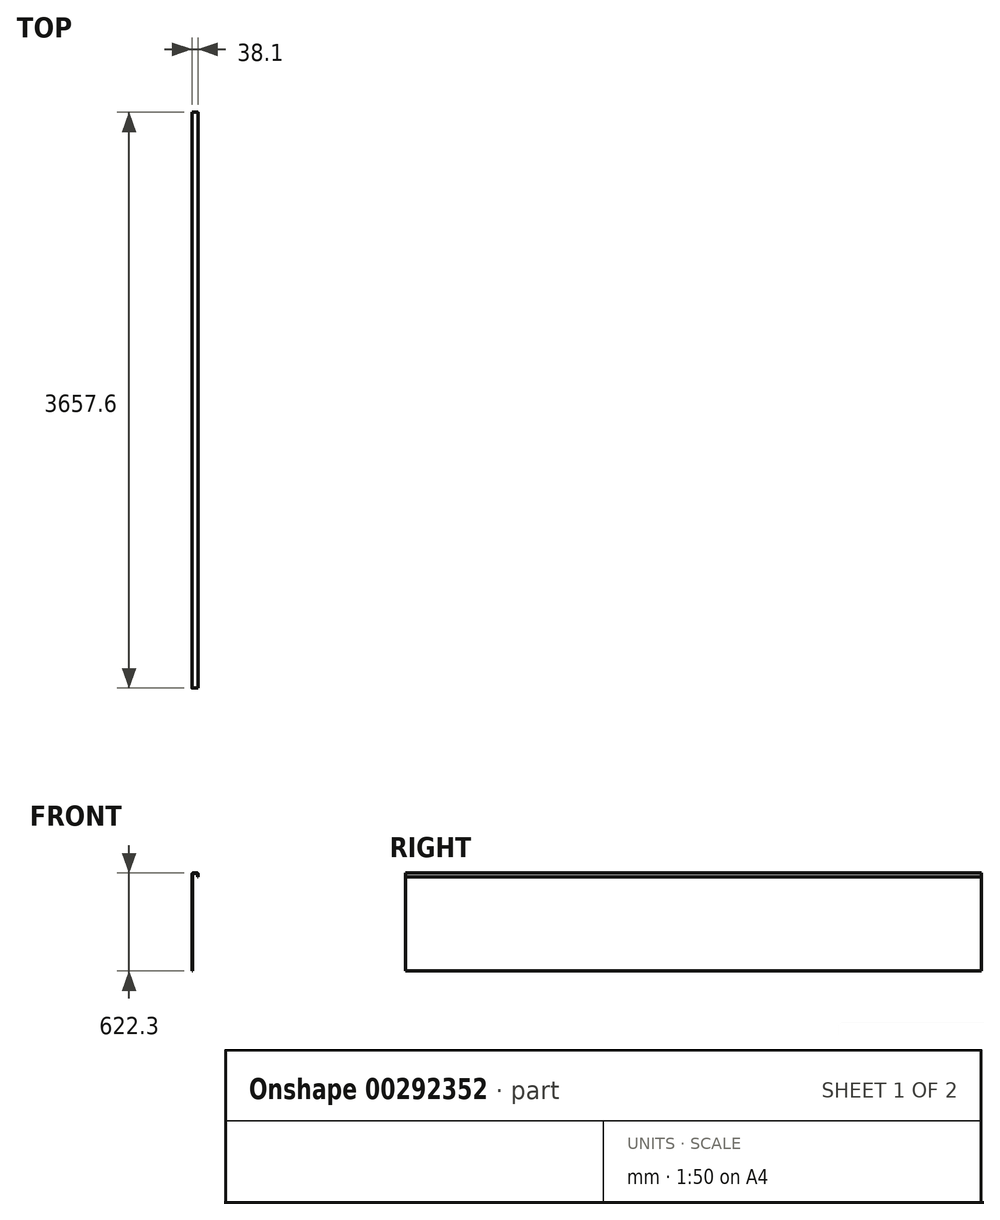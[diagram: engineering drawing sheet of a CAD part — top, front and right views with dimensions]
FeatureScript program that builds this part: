
annotation { "Feature Type Name" : "Feature", "Feature Type Description" : "" }
export const myFeature = defineFeature(function(context is Context, id is Id, definition is map)
    precondition{}
    {
        {
            var Q0;
            Q0=qCreatedBy(makeId("Front.planeOp"),FACE);
            var sketch = newSketch(context, id + "F0", { "sketchPlane" : qUnion([Q0])});
            skLineSegment(sketch, "E0", {"start": v(0, 0) * mm, "end": v(0, 616.97) * mm});
            skLineSegment(sketch, "E1", {"start": v(5.33, 622.3) * mm, "end": v(32.77, 622.3) * mm});
            skLineSegment(sketch, "E2", {"start": v(38.1, 616.97) * mm, "end": v(38.1, 596.9) * mm});
            skPoint(sketch, "E3.visualSharp", {"position": v(0, 622.3) * mm});
            skArc(sketch, "E3.filletArc", {"start": v(5.33, 622.3) * mm, "mid": v(1.56, 620.74) * mm, "end": v(0, 616.97) * mm});
            skPoint(sketch, "E4.visualSharp", {"position": v(38.1, 622.3) * mm});
            skArc(sketch, "E4.filletArc", {"start": v(38.1, 616.97) * mm, "mid": v(36.54, 620.74) * mm, "end": v(32.77, 622.3) * mm});
            skLineSegment(sketch, "E5.0", {"start": v(35.43, 616.97) * mm, "end": v(35.43, 596.9) * mm});
            skLineSegment(sketch, "E5.1", {"start": v(5.33, 619.63) * mm, "end": v(32.77, 619.63) * mm});
            skLineSegment(sketch, "E5.2", {"start": v(2.67, 0) * mm, "end": v(2.67, 616.97) * mm});
            skPoint(sketch, "E6.visualSharp", {"position": v(2.67, 619.63) * mm});
            skArc(sketch, "E6.filletArc", {"start": v(5.33, 619.63) * mm, "mid": v(3.45, 618.85) * mm, "end": v(2.67, 616.97) * mm});
            skPoint(sketch, "E7.visualSharp", {"position": v(35.43, 619.63) * mm});
            skArc(sketch, "E7.filletArc", {"start": v(35.43, 616.97) * mm, "mid": v(34.65, 618.85) * mm, "end": v(32.77, 619.63) * mm});
            skLineSegment(sketch, "E8", {"start": v(35.43, 596.9) * mm, "end": v(38.1, 596.9) * mm});
            skLineSegment(sketch, "E9", {"start": v(0, 0) * mm, "end": v(2.67, 0) * mm});
            skSolve(sketch);
        }
        {
            var Q0;
            Q0=makeQuery(id+"F0.imprint","IMPRINT",FACE,{"disambiguationData":[TD([[makeQuery(id+"F0.imprint","IMPRINT",EDGE,{"derivedFrom":sQuery(id+"F0.wireOp",EDGE,"E0")}),-1.0]])]});
            extrude(context, id + "F1", {"entities" : qUnion([Q0]), "oppositeDirection" : true, "depth" : 3657.6 * mm});
        }
    });
